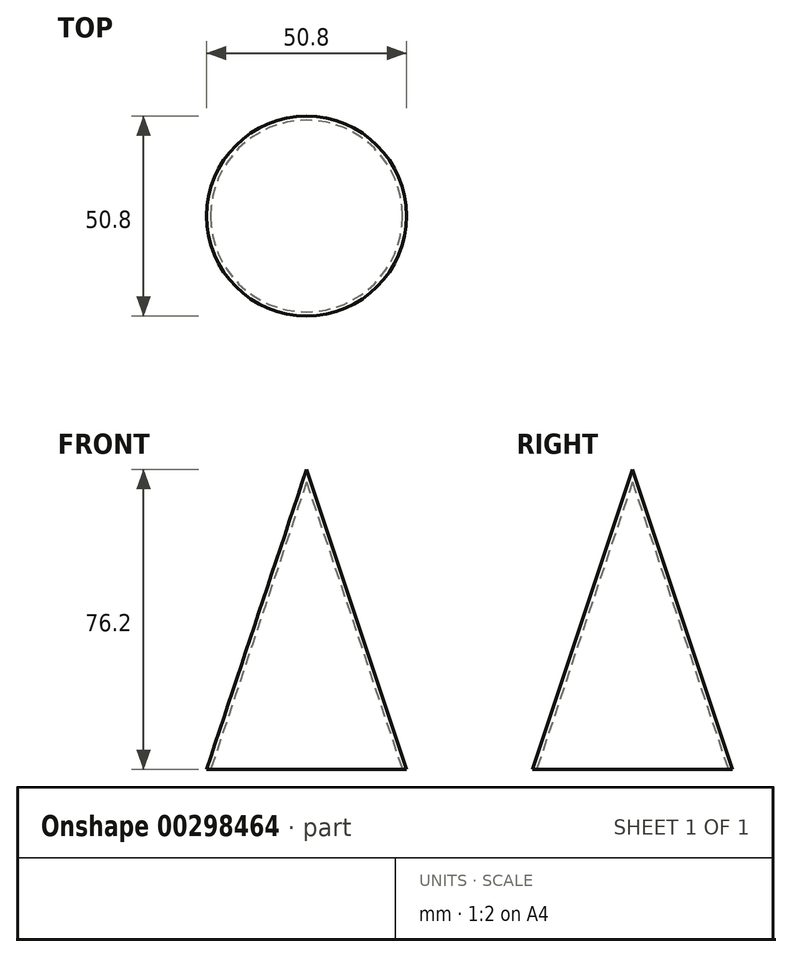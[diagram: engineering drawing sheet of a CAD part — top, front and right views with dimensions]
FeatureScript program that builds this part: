
annotation { "Feature Type Name" : "Feature", "Feature Type Description" : "" }
export const myFeature = defineFeature(function(context is Context, id is Id, definition is map)
    precondition{}
    {
        {
            var Q0;
            Q0=qCreatedBy(makeId("Front.planeOp"),FACE);
            var sketch = newSketch(context, id + "F0", { "sketchPlane" : qUnion([Q0])});
            skLineSegment(sketch, "E0", {"start": v(0, 0) * mm, "end": v(0, 76.2) * mm});
            skLineSegment(sketch, "E1", {"start": v(0, 76.2) * mm, "end": v(25.4, 0) * mm});
            skLineSegment(sketch, "E2", {"start": v(25.4, 0) * mm, "end": v(0, 0) * mm});
            skSolve(sketch);
        }
        {
            var Q0;
            Q0=makeQuery(id+"F0.imprint","IMPRINT",FACE,{"disambiguationData":[TD([[makeQuery(id+"F0.imprint","IMPRINT",EDGE,{"derivedFrom":sQuery(id+"F0.wireOp",EDGE,"E0")}),-1.0]])]});
            var Q1;
            Q1=sQuery(id+"F0.wireOp",EDGE,"E0");
            revolve(context, id + "F1", {"entities" : qUnion([Q0]), "axis" : qUnion([Q1]), "revolveType" : RevolveType.FULL});
        }
        {
            var Q0;
            Q0=makeQuery(id+"F1.opRevolve","SWEPT_FACE",FACE,{"disambiguationData":[OSD([sQuery(id+"F0.wireOp",EDGE,"E2")])]});
            shell(context, id + "F2", {"entities" : qUnion([Q0]), "thickness" : 1 * mm});
        }
    });
